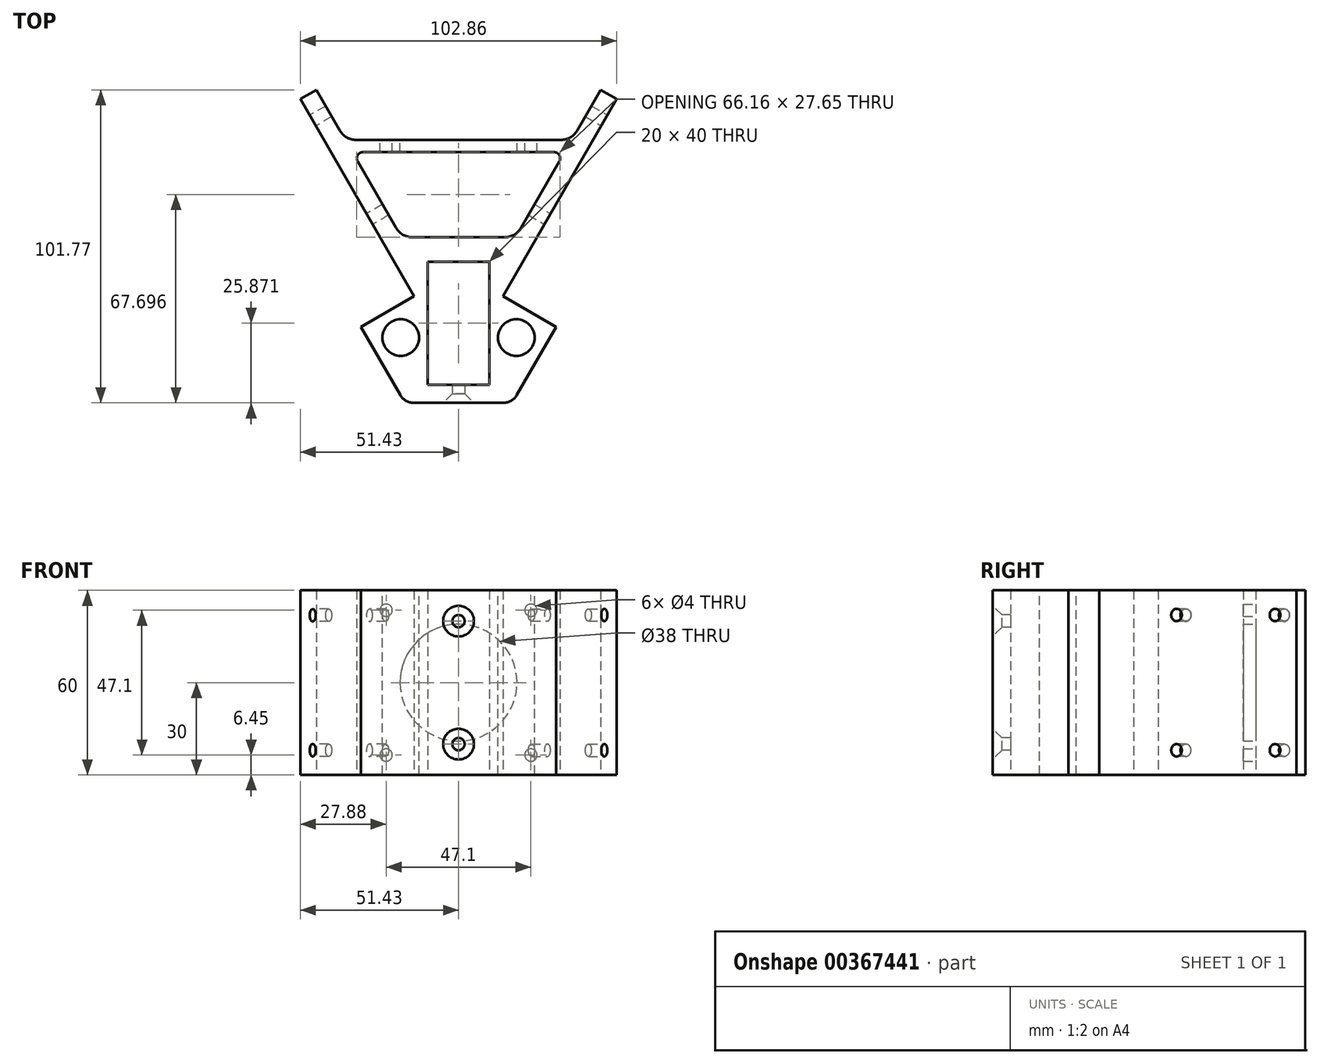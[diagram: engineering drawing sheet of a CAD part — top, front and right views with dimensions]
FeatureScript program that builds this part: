
annotation { "Feature Type Name" : "Feature", "Feature Type Description" : "" }
export const myFeature = defineFeature(function(context is Context, id is Id, definition is map)
    precondition{}
    {
        {
            var Q0;
            Q0=qCreatedBy(makeId("Top.planeOp"),FACE);
            var sketch = newSketch(context, id + "F0", { "sketchPlane" : qUnion([Q0])});
            skLineSegment(sketch, "E0", {"start": v(17.5, 30.31) * mm, "end": v(31.75, 55) * mm});
            skLineSegment(sketch, "E1", {"start": v(-17.5, 30.31) * mm, "end": v(-31.75, 55) * mm});
            skLineSegment(sketch, "E2", {"start": v(-17.5, 30.31) * mm, "end": v(17.5, 30.31) * mm});
            skLineSegment(sketch, "E3", {"start": v(-31.75, 55) * mm, "end": v(-14.43, 65) * mm});
            skLineSegment(sketch, "E4", {"start": v(-14.43, 65) * mm, "end": v(-51.43, 129.08) * mm});
            skLineSegment(sketch, "E5", {"start": v(-51.43, 129.08) * mm, "end": v(-46.23, 132.08) * mm});
            skLineSegment(sketch, "E6", {"start": v(31.75, 55) * mm, "end": v(14.43, 65) * mm});
            skLineSegment(sketch, "E7", {"start": v(14.43, 65) * mm, "end": v(51.43, 129.08) * mm});
            skLineSegment(sketch, "E8", {"start": v(51.43, 129.08) * mm, "end": v(46.23, 132.08) * mm});
            skLineSegment(sketch, "E9", {"start": v(-46.23, 132.08) * mm, "end": v(-36.85, 115.83) * mm});
            skLineSegment(sketch, "E10", {"start": v(18.58, 84.18) * mm, "end": v(34.54, 111.83) * mm});
            skLineSegment(sketch, "E11.bottom", {"start": v(-10, 36.18) * mm, "end": v(10, 36.18) * mm});
            skLineSegment(sketch, "E11.top", {"start": v(-10, 76.18) * mm, "end": v(10, 76.18) * mm});
            skLineSegment(sketch, "E11.left", {"start": v(-10, 36.18) * mm, "end": v(-10, 76.18) * mm});
            skLineSegment(sketch, "E11.right", {"start": v(10, 36.18) * mm, "end": v(10, 76.18) * mm});
            skLineSegment(sketch, "E12", {"start": v(36.85, 115.83) * mm, "end": v(-36.85, 115.83) * mm});
            skLineSegment(sketch, "E13.trimOffspring", {"start": v(36.85, 115.83) * mm, "end": v(46.23, 132.08) * mm});
            skLineSegment(sketch, "E14.trimOffspring", {"start": v(-34.54, 111.83) * mm, "end": v(-18.58, 84.18) * mm});
            skLineSegment(sketch, "E15", {"start": v(-34.54, 111.83) * mm, "end": v(34.54, 111.83) * mm});
            skLineSegment(sketch, "E16", {"start": v(18.58, 84.18) * mm, "end": v(-18.58, 84.18) * mm});
            skSolve(sketch);
        }
        {
            var Q0;
            Q0=qSketchRegion(id+"F0",true);
            extrude(context, id + "F1", {"entities" : qUnion([Q0]), "depth" : 60 * mm});
        }
        {
            var Q0;
            Q0=makeQuery(id+"F1.opExtrude","SWEPT_EDGE",EDGE,{"disambiguationData":[OSD([sQuery(id+"F0.wireOp",EDGE,"E1"),sQuery(id+"F0.wireOp",EDGE,"E2")])]});
            var Q1;
            Q1=makeQuery(id+"F1.opExtrude","SWEPT_EDGE",EDGE,{"disambiguationData":[OSD([sQuery(id+"F0.wireOp",EDGE,"E0"),sQuery(id+"F0.wireOp",EDGE,"E2")])]});
            fillet(context, id + "F2", {"entities" : qUnion([Q0, Q1]), "radius" : 5 * mm, "tangentPropagation" : true, "allowEdgeOverflow" : false});
        }
        {
            var Q0;
            Q0=makeQuery(id+"F1.opExtrude","SWEPT_EDGE",EDGE,{"disambiguationData":[OSD([sQuery(id+"F0.wireOp",EDGE,"E10"),sQuery(id+"F0.wireOp",EDGE,"E16")])]});
            var Q1;
            Q1=makeQuery(id+"F1.opExtrude","SWEPT_EDGE",EDGE,{"disambiguationData":[OSD([sQuery(id+"F0.wireOp",EDGE,"E14.trimOffspring"),sQuery(id+"F0.wireOp",EDGE,"E16")])]});
            var Q2;
            Q2=makeQuery(id+"F1.opExtrude","SWEPT_EDGE",EDGE,{"disambiguationData":[OSD([sQuery(id+"F0.wireOp",EDGE,"E9"),sQuery(id+"F0.wireOp",EDGE,"E12")])]});
            var Q3;
            Q3=makeQuery(id+"F1.opExtrude","SWEPT_EDGE",EDGE,{"disambiguationData":[OSD([sQuery(id+"F0.wireOp",EDGE,"E12"),sQuery(id+"F0.wireOp",EDGE,"E13.trimOffspring")])]});
            fillet(context, id + "F3", {"entities" : qUnion([Q0, Q1, Q2, Q3]), "radius" : 6 * mm, "tangentPropagation" : true, "allowEdgeOverflow" : false});
        }
        {
            var Q0;
            Q0=makeQuery(id+"F1.opExtrude","SWEPT_EDGE",EDGE,{"disambiguationData":[OSD([sQuery(id+"F0.wireOp",EDGE,"E10"),sQuery(id+"F0.wireOp",EDGE,"E15")])]});
            var Q1;
            Q1=makeQuery(id+"F1.opExtrude","SWEPT_EDGE",EDGE,{"disambiguationData":[OSD([sQuery(id+"F0.wireOp",EDGE,"E14.trimOffspring"),sQuery(id+"F0.wireOp",EDGE,"E15")])]});
            fillet(context, id + "F4", {"entities" : qUnion([Q0, Q1]), "radius" : 2 * mm, "tangentPropagation" : true, "allowEdgeOverflow" : false});
        }
        {
            var Q0;
            Q0=makeQuery(id+"F1.opExtrude","CAP_FACE",FACE,{"disambiguationData":[OSD([sQuery(id+"F0.wireOp",EDGE,"E0"),sQuery(id+"F0.wireOp",EDGE,"E1"),sQuery(id+"F0.wireOp",EDGE,"E2"),sQuery(id+"F0.wireOp",EDGE,"E3"),sQuery(id+"F0.wireOp",EDGE,"E4"),sQuery(id+"F0.wireOp",EDGE,"E5"),sQuery(id+"F0.wireOp",EDGE,"E6"),sQuery(id+"F0.wireOp",EDGE,"E7"),sQuery(id+"F0.wireOp",EDGE,"E8"),sQuery(id+"F0.wireOp",EDGE,"E9"),sQuery(id+"F0.wireOp",EDGE,"E10"),sQuery(id+"F0.wireOp",EDGE,"E11.bottom"),sQuery(id+"F0.wireOp",EDGE,"E11.top"),sQuery(id+"F0.wireOp",EDGE,"E11.left"),sQuery(id+"F0.wireOp",EDGE,"E11.right"),sQuery(id+"F0.wireOp",EDGE,"E12"),sQuery(id+"F0.wireOp",EDGE,"E13.trimOffspring"),sQuery(id+"F0.wireOp",EDGE,"E14.trimOffspring"),sQuery(id+"F0.wireOp",EDGE,"E15"),sQuery(id+"F0.wireOp",EDGE,"E16")])],"isStart":false});
            var sketch = newSketch(context, id + "F5", { "sketchPlane" : qUnion([Q0])});
            skCircle(sketch, "E17", {"center": v(-18.8, 51.52) * mm, "radius": 5.97 * mm});
            skCircle(sketch, "E18", {"center": v(18.8, 51.52) * mm, "radius": 5.97 * mm});
            skSolve(sketch);
        }
        {
            var Q0;
            Q0=qSketchRegion(id+"F5",true);
            extrude(context, id + "F6", {"entities" : qUnion([Q0]), "operationType" : NewBodyOperationType.REMOVE, "endBound" : BoundingType.THROUGH_ALL, "oppositeDirection" : true, "depth" : 25 * mm});
        }
        {
            var Q0;
            Q0=makeQuery(id+"F1.opExtrude","SWEPT_FACE",FACE,{"disambiguationData":[OSD([sQuery(id+"F0.wireOp",EDGE,"E12")])]});
            var sketch = newSketch(context, id + "F7", { "sketchPlane" : qUnion([Q0])});
            skPoint(sketch, "E19.orphan", {"position": v(0, 60) * mm});
            skPoint(sketch, "E20.trimOffspring.end.orphan", {"position": v(0, 0) * mm});
            skPoint(sketch, "E21", {"position": v(-23.55, 53.55) * mm});
            skPoint(sketch, "E22", {"position": v(23.55, 53.55) * mm});
            skPoint(sketch, "E23", {"position": v(23.55, 6.45) * mm});
            skPoint(sketch, "E24", {"position": v(-23.55, 6.45) * mm});
            skPoint(sketch, "E25", {"position": v(0, 30) * mm});
            skSolve(sketch);
        }
        {
            var Q0;
            Q0=sQuery(id+"F7.wireOp",VERTEX,"E21");
            var Q1;
            Q1=sQuery(id+"F7.wireOp",VERTEX,"E24");
            var Q2;
            Q2=sQuery(id+"F7.wireOp",VERTEX,"E23");
            var Q3;
            Q3=sQuery(id+"F7.wireOp",VERTEX,"E22");
            var Q4;
            Q4=makeQuery(id+"F1.opExtrude","SWEPT_BODY",BODY,{"disambiguationData":[OSD([sQuery(id+"F0.wireOp",EDGE,"E0"),sQuery(id+"F0.wireOp",EDGE,"E1"),sQuery(id+"F0.wireOp",EDGE,"E2"),sQuery(id+"F0.wireOp",EDGE,"E3"),sQuery(id+"F0.wireOp",EDGE,"E4"),sQuery(id+"F0.wireOp",EDGE,"E5"),sQuery(id+"F0.wireOp",EDGE,"E6"),sQuery(id+"F0.wireOp",EDGE,"E7"),sQuery(id+"F0.wireOp",EDGE,"E8"),sQuery(id+"F0.wireOp",EDGE,"E9"),sQuery(id+"F0.wireOp",EDGE,"E10"),sQuery(id+"F0.wireOp",EDGE,"E11.bottom"),sQuery(id+"F0.wireOp",EDGE,"E11.top"),sQuery(id+"F0.wireOp",EDGE,"E11.left"),sQuery(id+"F0.wireOp",EDGE,"E11.right"),sQuery(id+"F0.wireOp",EDGE,"E12"),sQuery(id+"F0.wireOp",EDGE,"E13.trimOffspring"),sQuery(id+"F0.wireOp",EDGE,"E14.trimOffspring"),sQuery(id+"F0.wireOp",EDGE,"E15"),sQuery(id+"F0.wireOp",EDGE,"E16")])]});
            hole(context, id + "F8", {"style" : HoleStyle.SIMPLE, "endStyle" : HoleEndStyle.BLIND, "holeDiameter" : 4 * mm, "holeDepth" : 12 * mm, "locations" : qUnion([Q0, Q1, Q2, Q3]), "scope" : qUnion([Q4])});
        }
        {
            var Q0;
            Q0=makeQuery(id+"F1.opExtrude","SWEPT_FACE",FACE,{"disambiguationData":[OSD([sQuery(id+"F0.wireOp",EDGE,"E12")])]});
            var sketch = newSketch(context, id + "F9", { "sketchPlane" : qUnion([Q0])});
            skCircle(sketch, "E26", {"center": v(0, 30) * mm, "radius": 19 * mm});
            skPoint(sketch, "E26.centerSnap0", {"position": v(-33.39, 30) * mm});
            skSolve(sketch);
        }
        {
            var Q0;
            Q0=qSketchRegion(id+"F9",true);
            extrude(context, id + "F10", {"entities" : qUnion([Q0]), "operationType" : NewBodyOperationType.REMOVE, "oppositeDirection" : true, "depth" : 25 * mm});
        }
        {
            var Q0;
            Q0=makeQuery(id+"F1.opExtrude","SWEPT_FACE",FACE,{"disambiguationData":[OSD([sQuery(id+"F0.wireOp",EDGE,"E7")])]});
            var sketch = newSketch(context, id + "F11", { "sketchPlane" : qUnion([Q0])});
            skPoint(sketch, "E27", {"position": v(129.5, 8) * mm});
            skPoint(sketch, "E28", {"position": v(129.5, 52) * mm});
            skPoint(sketch, "E29", {"position": v(92.5, 52) * mm});
            skPoint(sketch, "E30", {"position": v(92.5, 8) * mm});
            skSolve(sketch);
        }
        {
            var Q0;
            Q0=sQuery(id+"F11.wireOp",VERTEX,"E29");
            var Q1;
            Q1=sQuery(id+"F11.wireOp",VERTEX,"E28");
            var Q2;
            Q2=sQuery(id+"F11.wireOp",VERTEX,"E30");
            var Q3;
            Q3=sQuery(id+"F11.wireOp",VERTEX,"E27");
            var Q4;
            Q4=makeQuery(id+"F1.opExtrude","SWEPT_BODY",BODY,{"disambiguationData":[OSD([sQuery(id+"F0.wireOp",EDGE,"E0"),sQuery(id+"F0.wireOp",EDGE,"E1"),sQuery(id+"F0.wireOp",EDGE,"E2"),sQuery(id+"F0.wireOp",EDGE,"E3"),sQuery(id+"F0.wireOp",EDGE,"E4"),sQuery(id+"F0.wireOp",EDGE,"E5"),sQuery(id+"F0.wireOp",EDGE,"E6"),sQuery(id+"F0.wireOp",EDGE,"E7"),sQuery(id+"F0.wireOp",EDGE,"E8"),sQuery(id+"F0.wireOp",EDGE,"E9"),sQuery(id+"F0.wireOp",EDGE,"E10"),sQuery(id+"F0.wireOp",EDGE,"E11.bottom"),sQuery(id+"F0.wireOp",EDGE,"E11.top"),sQuery(id+"F0.wireOp",EDGE,"E11.left"),sQuery(id+"F0.wireOp",EDGE,"E11.right"),sQuery(id+"F0.wireOp",EDGE,"E12"),sQuery(id+"F0.wireOp",EDGE,"E13.trimOffspring"),sQuery(id+"F0.wireOp",EDGE,"E14.trimOffspring"),sQuery(id+"F0.wireOp",EDGE,"E15"),sQuery(id+"F0.wireOp",EDGE,"E16")])]});
            hole(context, id + "F12", {"style" : HoleStyle.SIMPLE, "endStyle" : HoleEndStyle.BLIND, "holeDiameter" : 4 * mm, "holeDepth" : 12 * mm, "locations" : qUnion([Q0, Q1, Q2, Q3]), "scope" : qUnion([Q4])});
        }
        {
            var Q0;
            Q0=makeQuery(id+"F1.opExtrude","SWEPT_FACE",FACE,{"disambiguationData":[OSD([sQuery(id+"F0.wireOp",EDGE,"E4")])]});
            var sketch = newSketch(context, id + "F13", { "sketchPlane" : qUnion([Q0])});
            skPoint(sketch, "E31", {"position": v(-129.5, 8) * mm});
            skPoint(sketch, "E32", {"position": v(-129.5, 51.9) * mm});
            skPoint(sketch, "E33", {"position": v(-92.5, 51.9) * mm});
            skPoint(sketch, "E34", {"position": v(-92.5, 8) * mm});
            skSolve(sketch);
        }
        {
            var Q0;
            Q0=sQuery(id+"F13.wireOp",VERTEX,"E34");
            var Q1;
            Q1=sQuery(id+"F13.wireOp",VERTEX,"E31");
            var Q2;
            Q2=sQuery(id+"F13.wireOp",VERTEX,"E33");
            var Q3;
            Q3=sQuery(id+"F13.wireOp",VERTEX,"E32");
            var Q4;
            Q4=makeQuery(id+"F1.opExtrude","SWEPT_BODY",BODY,{"disambiguationData":[OSD([sQuery(id+"F0.wireOp",EDGE,"E0"),sQuery(id+"F0.wireOp",EDGE,"E1"),sQuery(id+"F0.wireOp",EDGE,"E2"),sQuery(id+"F0.wireOp",EDGE,"E3"),sQuery(id+"F0.wireOp",EDGE,"E4"),sQuery(id+"F0.wireOp",EDGE,"E5"),sQuery(id+"F0.wireOp",EDGE,"E6"),sQuery(id+"F0.wireOp",EDGE,"E7"),sQuery(id+"F0.wireOp",EDGE,"E8"),sQuery(id+"F0.wireOp",EDGE,"E9"),sQuery(id+"F0.wireOp",EDGE,"E10"),sQuery(id+"F0.wireOp",EDGE,"E11.bottom"),sQuery(id+"F0.wireOp",EDGE,"E11.top"),sQuery(id+"F0.wireOp",EDGE,"E11.left"),sQuery(id+"F0.wireOp",EDGE,"E11.right"),sQuery(id+"F0.wireOp",EDGE,"E12"),sQuery(id+"F0.wireOp",EDGE,"E13.trimOffspring"),sQuery(id+"F0.wireOp",EDGE,"E14.trimOffspring"),sQuery(id+"F0.wireOp",EDGE,"E15"),sQuery(id+"F0.wireOp",EDGE,"E16")])]});
            hole(context, id + "F14", {"style" : HoleStyle.SIMPLE, "endStyle" : HoleEndStyle.BLIND, "holeDiameter" : 4 * mm, "holeDepth" : 12 * mm, "locations" : qUnion([Q0, Q1, Q2, Q3]), "scope" : qUnion([Q4])});
        }
        {
            var Q0;
            Q0=makeQuery(id+"F1.opExtrude","SWEPT_FACE",FACE,{"disambiguationData":[OSD([sQuery(id+"F0.wireOp",EDGE,"E2")])]});
            var sketch = newSketch(context, id + "F15", { "sketchPlane" : qUnion([Q0])});
            skPoint(sketch, "E35", {"position": v(0, 10) * mm});
            skPoint(sketch, "E36", {"position": v(0, 50) * mm});
            skSolve(sketch);
        }
        {
            var Q0;
            Q0=sQuery(id+"F15.wireOp",VERTEX,"E35");
            var Q1;
            Q1=sQuery(id+"F15.wireOp",VERTEX,"E36");
            var Q2;
            Q2=makeQuery(id+"F1.opExtrude","SWEPT_BODY",BODY,{"disambiguationData":[OSD([sQuery(id+"F0.wireOp",EDGE,"E0"),sQuery(id+"F0.wireOp",EDGE,"E1"),sQuery(id+"F0.wireOp",EDGE,"E2"),sQuery(id+"F0.wireOp",EDGE,"E3"),sQuery(id+"F0.wireOp",EDGE,"E4"),sQuery(id+"F0.wireOp",EDGE,"E5"),sQuery(id+"F0.wireOp",EDGE,"E6"),sQuery(id+"F0.wireOp",EDGE,"E7"),sQuery(id+"F0.wireOp",EDGE,"E8"),sQuery(id+"F0.wireOp",EDGE,"E9"),sQuery(id+"F0.wireOp",EDGE,"E10"),sQuery(id+"F0.wireOp",EDGE,"E11.bottom"),sQuery(id+"F0.wireOp",EDGE,"E11.top"),sQuery(id+"F0.wireOp",EDGE,"E11.left"),sQuery(id+"F0.wireOp",EDGE,"E11.right"),sQuery(id+"F0.wireOp",EDGE,"E12"),sQuery(id+"F0.wireOp",EDGE,"E13.trimOffspring"),sQuery(id+"F0.wireOp",EDGE,"E14.trimOffspring"),sQuery(id+"F0.wireOp",EDGE,"E15"),sQuery(id+"F0.wireOp",EDGE,"E16")])]});
            hole(context, id + "F16", {"style" : HoleStyle.C_SINK, "endStyle" : HoleEndStyle.BLIND, "holeDiameter" : 4 * mm, "cSinkDiameter" : 10 * mm, "cSinkAngle" : 90 * degree, "holeDepth" : 12 * mm, "locations" : qUnion([Q0, Q1]), "scope" : qUnion([Q2])});
        }
    });
